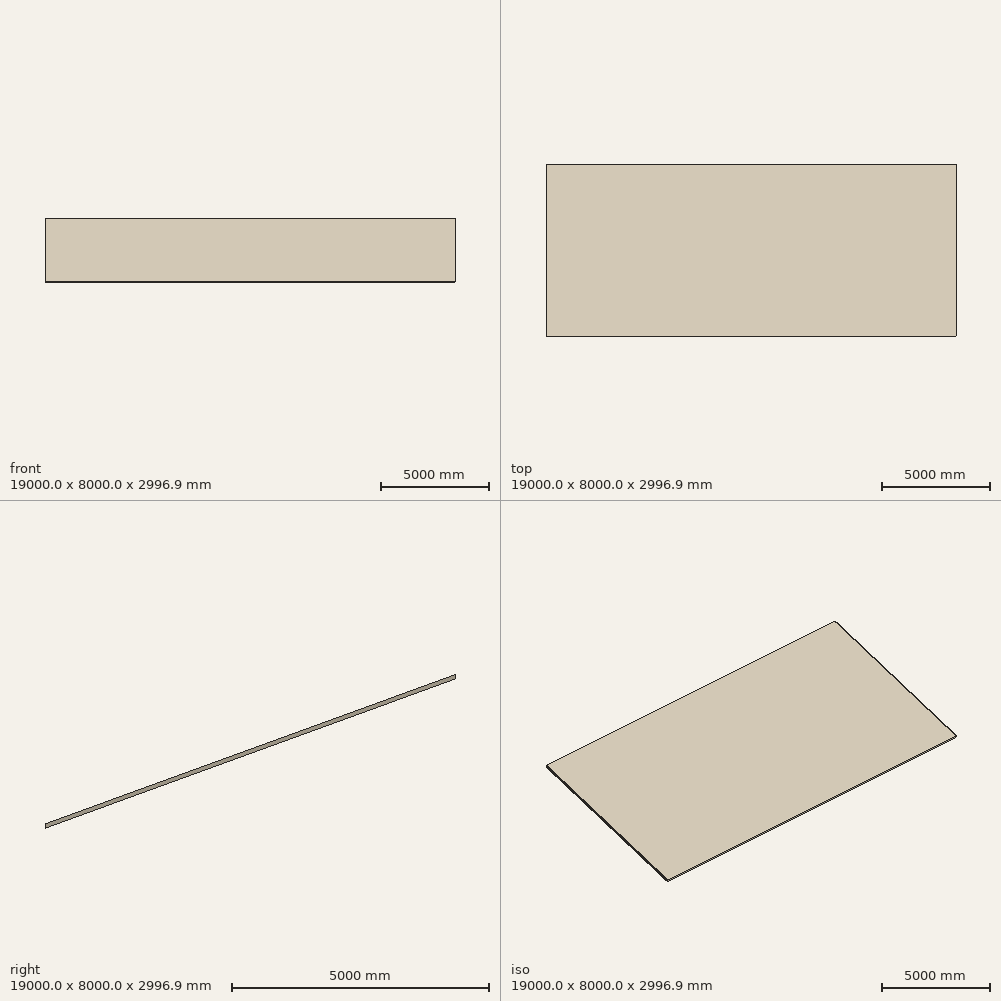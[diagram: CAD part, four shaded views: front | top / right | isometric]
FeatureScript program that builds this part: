
annotation { "Feature Type Name" : "Feature", "Feature Type Description" : "" }
export const myFeature = defineFeature(function(context is Context, id is Id, definition is map)
    precondition{}
    {
        {
            var Q0;
            Q0=qCreatedBy(makeId("Right.planeOp"),FACE);
            var sketch = newSketch(context, id + "F0", { "sketchPlane" : qUnion([Q0])});
            skLineSegment(sketch, "E0", {"start": v(0, 0) * mm, "end": v(-8000, -2911.76) * mm});
            skLineSegment(sketch, "E1", {"start": v(0, 0) * mm, "end": v(477.52, 0) * mm, "construction": true});
            skLineSegment(sketch, "E2.0", {"start": v(0, 85.13) * mm, "end": v(-8000, -2826.63) * mm});
            skLineSegment(sketch, "E3", {"start": v(-8000, -2826.63) * mm, "end": v(-8000, -2911.76) * mm});
            skLineSegment(sketch, "E4", {"start": v(0, 85.13) * mm, "end": v(0, 0) * mm});
            skSolve(sketch);
        }
        {
            var Q0;
            Q0 = qSketchRegion(id + "F0", true);
            extrude(context, id + "F1", {"entities" : qUnion([Q0]), "depth" : 19000 * mm});
        }
    });
